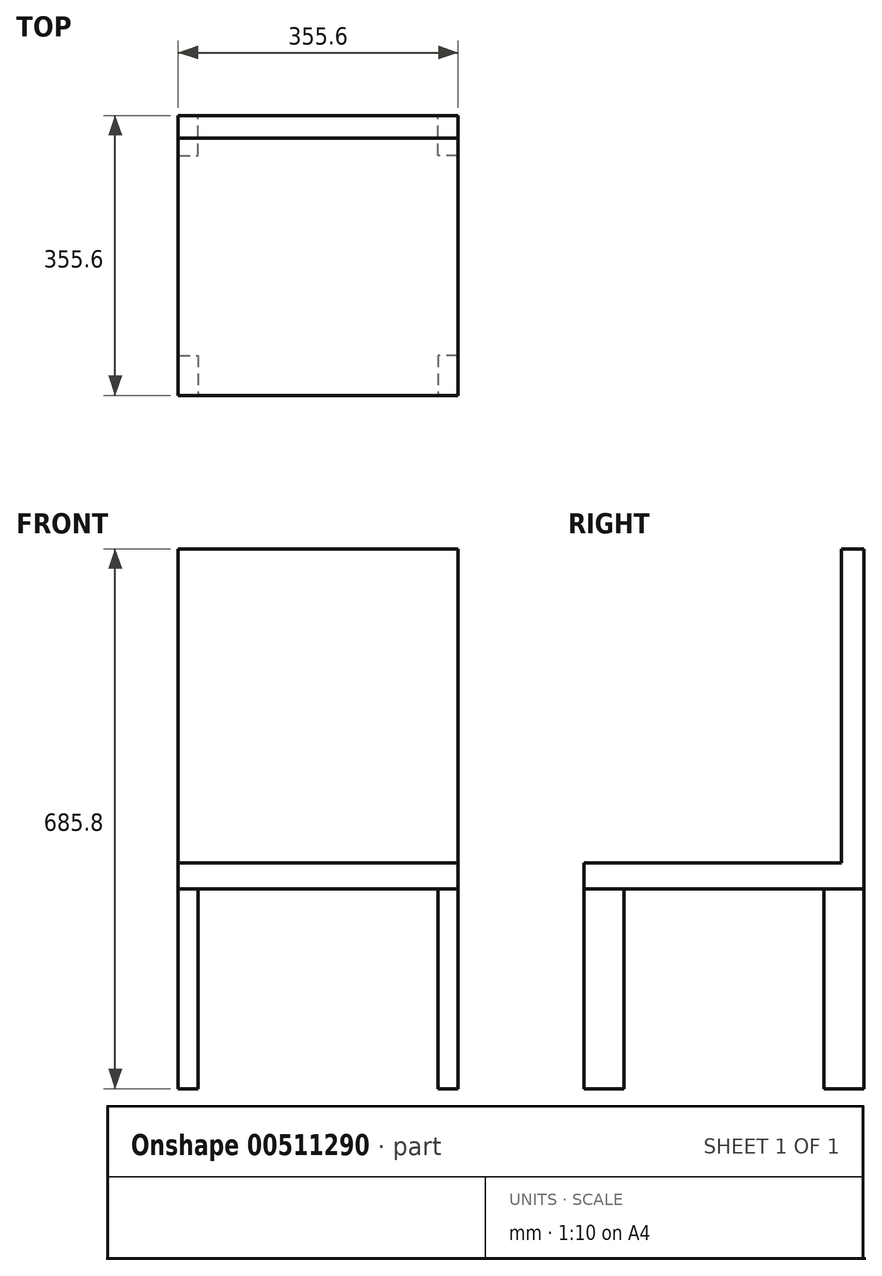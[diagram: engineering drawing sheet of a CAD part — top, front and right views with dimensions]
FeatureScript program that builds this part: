
annotation { "Feature Type Name" : "Feature", "Feature Type Description" : "" }
export const myFeature = defineFeature(function(context is Context, id is Id, definition is map)
    precondition{}
    {
        {
            var Q0;
            Q0=qCreatedBy(makeId("Top.planeOp"),FACE);
            var sketch = newSketch(context, id + "F0", { "sketchPlane" : qUnion([Q0])});
            skLineSegment(sketch, "E0", {"start": v(0, 0) * mm, "end": v(0, 50.8) * mm});
            skLineSegment(sketch, "E1", {"start": v(0, 50.8) * mm, "end": v(25.4, 50.8) * mm});
            skLineSegment(sketch, "E2", {"start": v(25.4, 50.8) * mm, "end": v(25.4, 0) * mm});
            skLineSegment(sketch, "E3", {"start": v(25.4, 0) * mm, "end": v(0, 0) * mm});
            skSolve(sketch);
        }
        {
            var Q0;
            Q0 = qSketchRegion(id + "F0", true);
            extrude(context, id + "F1", {"entities" : qUnion([Q0]), "depth" : 254 * mm});
        }
        {
            var Q0;
            Q0=makeQuery(id+"F1.opExtrude","CAP_FACE",FACE,{"disambiguationData":[OSD([sQuery(id+"F0.wireOp",EDGE,"E0"),sQuery(id+"F0.wireOp",EDGE,"E1"),sQuery(id+"F0.wireOp",EDGE,"E2"),sQuery(id+"F0.wireOp",EDGE,"E3")])],"isStart":false});
            var sketch = newSketch(context, id + "F2", { "sketchPlane" : qUnion([Q0])});
            skLineSegment(sketch, "E4", {"start": v(0, 0) * mm, "end": v(355.6, 0) * mm});
            skLineSegment(sketch, "E5", {"start": v(355.6, 0) * mm, "end": v(355.6, 355.6) * mm});
            skLineSegment(sketch, "E6", {"start": v(355.6, 355.6) * mm, "end": v(0, 355.6) * mm});
            skLineSegment(sketch, "E7", {"start": v(0, 355.6) * mm, "end": v(0, 0) * mm});
            skLineSegment(sketch, "E8", {"start": v(177.8, 355.6) * mm, "end": v(177.8, 0) * mm, "construction": true});
            skLineSegment(sketch, "E9", {"start": v(355.6, 177.8) * mm, "end": v(0, 177.8) * mm});
            skSolve(sketch);
        }
        {
            var Q0;
            Q0=sQuery(id+"F2.wireOp",EDGE,"E8");
            cPlane(context, id + "F3", {"entities" : qUnion([Q0]), "cplaneType" : CPlaneType.LINE_ANGLE, "offset" : 25.4 * mm, "angle" : 90 * degree, "width" : 152.4 * mm, "height" : 152.4 * mm});
        }
        {
            var Q0;
            Q0=makeQuery(id+"F1.opExtrude","SWEPT_BODY",BODY,{"disambiguationData":[OSD([sQuery(id+"F0.wireOp",EDGE,"E0"),sQuery(id+"F0.wireOp",EDGE,"E1"),sQuery(id+"F0.wireOp",EDGE,"E2"),sQuery(id+"F0.wireOp",EDGE,"E3")])]});
            var Q1;
            Q1=qCreatedBy(id+"F3.planeOp",FACE);
            mirror(context, id + "F4", {"entities" : qUnion([Q0]), "mirrorPlane" : qUnion([Q1])});
        }
        {
            var Q0;
            {var subQ0=sQuery(id+"F2.wireOp",EDGE,"E6");Q0=makeQuery(id+"F2.imprint","IMPRINT",FACE,{"disambiguationData":[TD([[makeQuery(id+"F2.imprint","IMPRINT",EDGE,{"derivedFrom":subQ0}),1.0]])]});}
            var Q1;
            {var subQ0=sQuery(id+"F2.wireOp",EDGE,"E9");Q1=makeQuery(id+"F2.imprint","IMPRINT",FACE,{"disambiguationData":[TD([[makeQuery(id+"F2.imprint","IMPRINT",EDGE,{"derivedFrom":subQ0}),1.0]])]});}
            var Q2;
            {var subQ4=makeQuery(id+"F1.opExtrude","CAP_EDGE",EDGE,{"disambiguationData":[OSD([sQuery(id+"F0.wireOp",EDGE,"E1")])],"isStart":false});Q2=makeQuery(id+"F2.imprint","IMPRINT",FACE,{"disambiguationData":[TD([[makeQuery(id+"F2.imprint","IMPRINT",EDGE,{"derivedFrom":subQ4}),-1.0]])]});}
            extrude(context, id + "F5", {"entities" : qUnion([Q0, Q1, Q2]), "depth" : 33.02 * mm});
        }
        {
            var Q0;
            Q0=sQuery(id+"F2.wireOp",EDGE,"E9");
            cPlane(context, id + "F6", {"entities" : qUnion([Q0]), "cplaneType" : CPlaneType.LINE_ANGLE, "offset" : 25.4 * mm, "angle" : 0 * degree, "width" : 152.4 * mm, "height" : 152.4 * mm});
        }
        {
            var Q0;
            Q0=makeQuery(id+"F1.opExtrude","SWEPT_BODY",BODY,{"disambiguationData":[OSD([sQuery(id+"F0.wireOp",EDGE,"E0"),sQuery(id+"F0.wireOp",EDGE,"E1"),sQuery(id+"F0.wireOp",EDGE,"E2"),sQuery(id+"F0.wireOp",EDGE,"E3")])]});
            var Q1;
            Q1=makeQuery(id+"F4.opPattern","COPY",BODY,{"derivedFrom":makeQuery(id+"F1.opExtrude","SWEPT_BODY",BODY,{"disambiguationData":[OSD([sQuery(id+"F0.wireOp",EDGE,"E0"),sQuery(id+"F0.wireOp",EDGE,"E1"),sQuery(id+"F0.wireOp",EDGE,"E2"),sQuery(id+"F0.wireOp",EDGE,"E3")])]}),"instanceName":"1"});
            var Q2;
            Q2=qCreatedBy(id+"F6.planeOp",FACE);
            mirror(context, id + "F7", {"entities" : qUnion([Q0, Q1]), "mirrorPlane" : qUnion([Q2])});
        }
        {
            var Q0;
            Q0=makeQuery(id+"F5.opExtrude","CAP_FACE",FACE,{"disambiguationData":[OSD([sQuery(id+"F2.wireOp",EDGE,"E4"),sQuery(id+"F2.wireOp",EDGE,"E5"),sQuery(id+"F2.wireOp",EDGE,"E6"),sQuery(id+"F2.wireOp",EDGE,"E7")])],"isStart":false});
            var sketch = newSketch(context, id + "F8", { "sketchPlane" : qUnion([Q0])});
            skLineSegment(sketch, "E10", {"start": v(0, 355.6) * mm, "end": v(0, 326.69) * mm});
            skLineSegment(sketch, "E11", {"start": v(0, 326.69) * mm, "end": v(355.6, 326.69) * mm});
            skLineSegment(sketch, "E12", {"start": v(355.6, 326.69) * mm, "end": v(355.6, 355.6) * mm});
            skLineSegment(sketch, "E13", {"start": v(355.6, 355.6) * mm, "end": v(0, 355.6) * mm});
            skSolve(sketch);
        }
        {
            var Q0;
            Q0=makeQuery(id+"F8.imprint","IMPRINT",FACE,{"disambiguationData":[TD([[makeQuery(id+"F8.imprint","IMPRINT",EDGE,{"derivedFrom":sQuery(id+"F8.wireOp",EDGE,"E10")}),1.0]])]});
            extrude(context, id + "F9", {"entities" : qUnion([Q0]), "operationType" : NewBodyOperationType.ADD, "depth" : 398.78 * mm});
        }
    });
